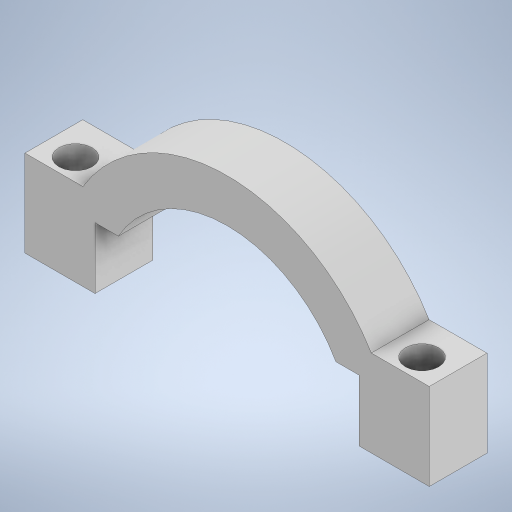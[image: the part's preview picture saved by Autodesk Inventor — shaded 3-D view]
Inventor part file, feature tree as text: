
AUTODESK INVENTOR PART (.ipt)
format: ipt  version: 2023.1 (Build 271208000, 208)  size: 248,832 bytes
history: native  units: mm
features: extrude x2, sketch x2, other x1
ambient origin geometry x8: Origin, YZ Plane, XZ Plane, XY Plane, X Axis, Y Axis, Z Axis, Center Point
bodies: Body1 (feature_tree)
feature tree (5):
  other  "솔리드1"
  extrude  "돌출1"  Depth=28.0mm
  extrude  "돌출2"  Depth=17.3mm
  sketch  "스케치1"
  sketch  "스케치2"
